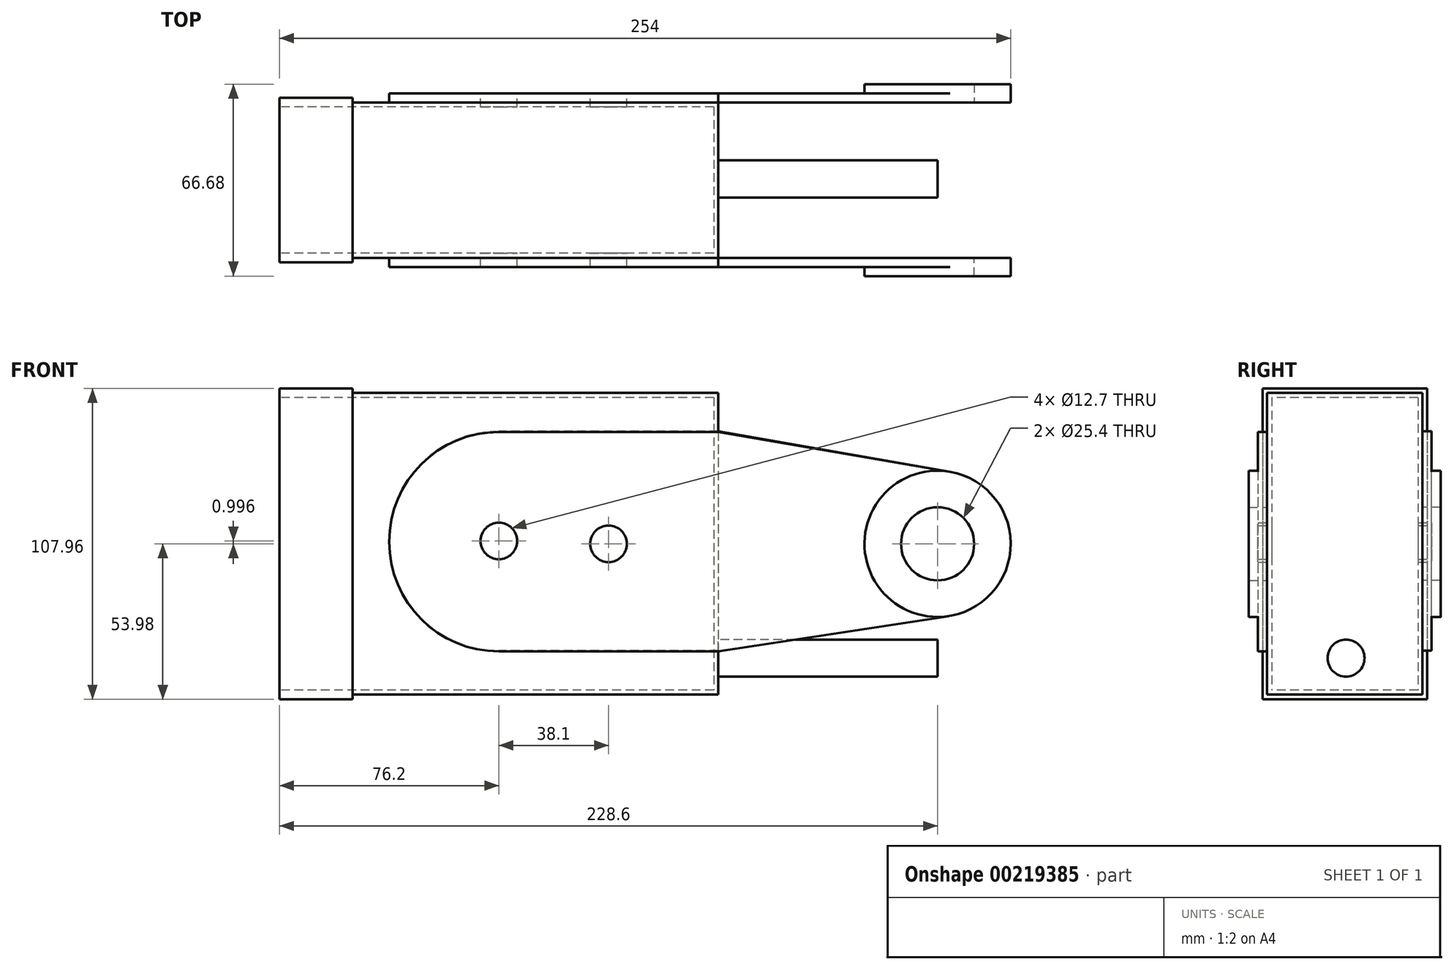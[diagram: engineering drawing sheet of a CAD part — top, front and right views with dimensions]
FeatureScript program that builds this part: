
annotation { "Feature Type Name" : "Feature", "Feature Type Description" : "" }
export const myFeature = defineFeature(function(context is Context, id is Id, definition is map)
    precondition{}
    {
        {
            var Q0;
            Q0=qCreatedBy(makeId("Right.planeOp"),FACE);
            var sketch = newSketch(context, id + "F0", { "sketchPlane" : qUnion([Q0])});
            skLineSegment(sketch, "E0.bottom", {"start": v(25.4, 50.8) * mm, "end": v(-25.4, 50.8) * mm});
            skLineSegment(sketch, "E0.top", {"start": v(25.4, -50.8) * mm, "end": v(-25.4, -50.8) * mm});
            skLineSegment(sketch, "E0.left", {"start": v(25.4, 50.8) * mm, "end": v(25.4, -50.8) * mm});
            skLineSegment(sketch, "E0.right", {"start": v(-25.4, 50.8) * mm, "end": v(-25.4, -50.8) * mm});
            skPoint(sketch, "E0.middle", {"position": v(0, 0) * mm});
            skLineSegment(sketch, "E1.0", {"start": v(26.99, 52.39) * mm, "end": v(-26.99, 52.39) * mm});
            skLineSegment(sketch, "E1.1", {"start": v(26.99, 52.39) * mm, "end": v(26.99, -52.39) * mm});
            skLineSegment(sketch, "E1.2", {"start": v(26.99, -52.39) * mm, "end": v(-26.99, -52.39) * mm});
            skLineSegment(sketch, "E1.3", {"start": v(-26.99, 52.39) * mm, "end": v(-26.99, -52.39) * mm});
            skSolve(sketch);
        }
        {
            var Q0;
            Q0=makeQuery(id+"F0.imprint","IMPRINT",FACE,{"disambiguationData":[TD([[makeQuery(id+"F0.imprint","IMPRINT",EDGE,{"derivedFrom":sQuery(id+"F0.wireOp",EDGE,"E0.bottom")}),-1.0]])]});
            extrude(context, id + "F1", {"entities" : qUnion([Q0]), "depth" : 152.4 * mm});
        }
        {
            var Q0;
            Q0=makeQuery(id+"F1.opExtrude","SWEPT_FACE",FACE,{"disambiguationData":[OSD([sQuery(id+"F0.wireOp",EDGE,"E1.1")])]});
            var sketch = newSketch(context, id + "F2", { "sketchPlane" : qUnion([Q0])});
            skLineSegment(sketch, "E2", {"start": v(-76.2, 52.39) * mm, "end": v(-76.2, -52.39) * mm, "construction": true});
            skLineSegment(sketch, "E3", {"start": v(0, 0) * mm, "end": v(-152.4, 0) * mm, "construction": true});
            skLineSegment(sketch, "E4", {"start": v(-152.4, 0) * mm, "end": v(-304.8, 0) * mm});
            skCircle(sketch, "E5", {"center": v(-228.6, 0) * mm, "radius": 12.7 * mm});
            skCircle(sketch, "E6", {"center": v(-228.6, 0) * mm, "radius": 25.4 * mm});
            skLineSegment(sketch, "E7", {"start": v(-152.4, 39.1) * mm, "end": v(-232.97, 25.02) * mm});
            skLineSegment(sketch, "E8", {"start": v(-152.4, -37.1) * mm, "end": v(-232.36, -25.12) * mm});
            skLineSegment(sketch, "E9", {"start": v(-152.4, 39.1) * mm, "end": v(-76.2, 39.1) * mm});
            skLineSegment(sketch, "E10", {"start": v(-152.4, -37.1) * mm, "end": v(-76.2, -37.1) * mm});
            skArc(sketch, "E11", {"start": v(-76.2, -37.1) * mm, "mid": v(-38.1, 1) * mm, "end": v(-76.2, 39.1) * mm});
            skSolve(sketch);
        }
        {
            var Q0;
            Q0 = qSketchRegion(id + "F2", true);
            extrude(context, id + "F3", {"entities" : qUnion([Q0]), "operationType" : NewBodyOperationType.ADD, "depth" : 3.17 * mm});
        }
        {
            var Q0;
            Q0=makeQuery(id+"F1.opExtrude","SWEPT_FACE",FACE,{"disambiguationData":[OSD([sQuery(id+"F0.wireOp",EDGE,"E1.3")])]});
            var sketch = newSketch(context, id + "F4", { "sketchPlane" : qUnion([Q0])});
            skLineSegment(sketch, "E12", {"start": v(152.4, 0) * mm, "end": v(293.28, 0) * mm});
            skPoint(sketch, "E12.endSnap0", {"position": v(152.4, 0) * mm});
            skCircle(sketch, "E13", {"center": v(228.6, 0) * mm, "radius": 12.7 * mm});
            skCircle(sketch, "E14", {"center": v(228.6, 0) * mm, "radius": 25.4 * mm});
            skLineSegment(sketch, "E15", {"start": v(152.4, 38.84) * mm, "end": v(232.9, 25.03) * mm});
            skLineSegment(sketch, "E16", {"start": v(152.4, -37.36) * mm, "end": v(232.44, -25.1) * mm});
            skLineSegment(sketch, "E17", {"start": v(152.4, 38.84) * mm, "end": v(76.2, 38.84) * mm});
            skLineSegment(sketch, "E18", {"start": v(152.4, -37.36) * mm, "end": v(76.2, -37.36) * mm});
            skLineSegment(sketch, "E19", {"start": v(76.2, 38.84) * mm, "end": v(76.2, -37.36) * mm, "construction": true});
            skArc(sketch, "E20", {"start": v(76.2, 38.84) * mm, "mid": v(38.1, 0.74) * mm, "end": v(76.2, -37.36) * mm});
            skSolve(sketch);
        }
        {
            var Q0;
            Q0 = qSketchRegion(id + "F4", true);
            extrude(context, id + "F5", {"entities" : qUnion([Q0]), "operationType" : NewBodyOperationType.ADD, "depth" : 3.17 * mm});
        }
        {
            var Q0;
            Q0=qCreatedBy(makeId("Right.planeOp"),FACE);
            var sketch = newSketch(context, id + "F6", { "sketchPlane" : qUnion([Q0])});
            skLineSegment(sketch, "E21.0", {"start": v(28.58, 53.97) * mm, "end": v(-28.57, 53.97) * mm});
            skLineSegment(sketch, "E21.1", {"start": v(28.58, 53.97) * mm, "end": v(28.58, -53.98) * mm});
            skLineSegment(sketch, "E21.2", {"start": v(28.58, -53.98) * mm, "end": v(-28.58, -53.98) * mm});
            skLineSegment(sketch, "E21.3", {"start": v(-28.57, 53.97) * mm, "end": v(-28.58, -53.98) * mm});
            skLineSegment(sketch, "E22.0", {"start": v(26.99, 52.39) * mm, "end": v(-26.99, 52.39) * mm});
            skLineSegment(sketch, "E22.1", {"start": v(26.99, 52.39) * mm, "end": v(26.99, -52.39) * mm});
            skLineSegment(sketch, "E22.2", {"start": v(26.99, -52.39) * mm, "end": v(-26.99, -52.39) * mm});
            skLineSegment(sketch, "E22.3", {"start": v(-26.99, 52.39) * mm, "end": v(-26.99, -52.39) * mm});
            skSolve(sketch);
        }
        {
            var Q0;
            Q0=makeQuery(id+"F6.imprint","IMPRINT",FACE,{"disambiguationData":[TD([[makeQuery(id+"F6.imprint","IMPRINT",EDGE,{"derivedFrom":sQuery(id+"F6.wireOp",EDGE,"E21.0")}),1.0]])]});
            extrude(context, id + "F7", {"entities" : qUnion([Q0]), "operationType" : NewBodyOperationType.ADD, "depth" : 25.4 * mm});
        }
        {
            var Q0;
            Q0=makeQuery(id+"F3.opExtrude","CAP_FACE",FACE,{"disambiguationData":[OSD([sQuery(id+"F2.wireOp",EDGE,"E5"),sQuery(id+"F2.wireOp",EDGE,"E6"),sQuery(id+"F2.wireOp",EDGE,"E7"),sQuery(id+"F2.wireOp",EDGE,"E8"),sQuery(id+"F2.wireOp",EDGE,"E9"),sQuery(id+"F2.wireOp",EDGE,"E10"),sQuery(id+"F2.wireOp",EDGE,"E11")])],"isStart":false});
            var sketch = newSketch(context, id + "F8", { "sketchPlane" : qUnion([Q0])});
            skCircle(sketch, "E23", {"center": v(-114.3, 0) * mm, "radius": 6.35 * mm});
            skCircle(sketch, "E24", {"center": v(-76.2, 1) * mm, "radius": 6.35 * mm});
            skSolve(sketch);
        }
        {
            var Q0;
            Q0=makeQuery(id+"F8.imprint","IMPRINT",FACE,{"disambiguationData":[TD([[makeQuery(id+"F8.imprint","IMPRINT",EDGE,{"derivedFrom":sQuery(id+"F8.wireOp",EDGE,"E23")}),1.0]])]});
            var Q1;
            Q1=makeQuery(id+"F8.imprint","IMPRINT",FACE,{"disambiguationData":[TD([[makeQuery(id+"F8.imprint","IMPRINT",EDGE,{"derivedFrom":sQuery(id+"F8.wireOp",EDGE,"E24")}),1.0]])]});
            extrude(context, id + "F9", {"entities" : qUnion([Q0, Q1]), "operationType" : NewBodyOperationType.REMOVE, "oppositeDirection" : true, "depth" : 152.4 * mm});
        }
        {
            var Q0;
            Q0=makeQuery(id+"F1.opExtrude","CAP_FACE",FACE,{"disambiguationData":[OSD([sQuery(id+"F0.wireOp",EDGE,"E0.bottom"),sQuery(id+"F0.wireOp",EDGE,"E0.top"),sQuery(id+"F0.wireOp",EDGE,"E0.left"),sQuery(id+"F0.wireOp",EDGE,"E0.right"),sQuery(id+"F0.wireOp",EDGE,"E1.0"),sQuery(id+"F0.wireOp",EDGE,"E1.1"),sQuery(id+"F0.wireOp",EDGE,"E1.2"),sQuery(id+"F0.wireOp",EDGE,"E1.3")])],"isStart":false});
            var sketch = newSketch(context, id + "F10", { "sketchPlane" : qUnion([Q0])});
            skLineSegment(sketch, "E25.bottom", {"start": v(25.4, 50.8) * mm, "end": v(-25.4, 50.8) * mm});
            skLineSegment(sketch, "E25.top", {"start": v(25.4, -50.8) * mm, "end": v(-25.4, -50.8) * mm});
            skLineSegment(sketch, "E25.left", {"start": v(25.4, 50.8) * mm, "end": v(25.4, -50.8) * mm});
            skLineSegment(sketch, "E25.right", {"start": v(-25.4, 50.8) * mm, "end": v(-25.4, -50.8) * mm});
            skPoint(sketch, "E25.middle", {"position": v(0, 0) * mm});
            skSolve(sketch);
        }
        {
            var Q0;
            Q0 = qSketchRegion(id + "F10", true);
            extrude(context, id + "F11", {"entities" : qUnion([Q0]), "operationType" : NewBodyOperationType.ADD, "oppositeDirection" : true, "depth" : 1.59 * mm});
        }
        {
            var Q0;
            Q0=makeQuery(id+"F5.opExtrude","CAP_FACE",FACE,{"disambiguationData":[OSD([sQuery(id+"F4.wireOp",EDGE,"E13"),sQuery(id+"F4.wireOp",EDGE,"E14"),sQuery(id+"F4.wireOp",EDGE,"E15"),sQuery(id+"F4.wireOp",EDGE,"E16"),sQuery(id+"F4.wireOp",EDGE,"E17"),sQuery(id+"F4.wireOp",EDGE,"E18"),sQuery(id+"F4.wireOp",EDGE,"E20")])],"isStart":false});
            var sketch = newSketch(context, id + "F12", { "sketchPlane" : qUnion([Q0])});
            skCircle(sketch, "E26", {"center": v(228.6, 0) * mm, "radius": 25.4 * mm});
            skCircle(sketch, "E27", {"center": v(228.6, 0) * mm, "radius": 12.7 * mm});
            skSolve(sketch);
        }
        {
            var Q0;
            Q0 = qSketchRegion(id + "F12", true);
            extrude(context, id + "F13", {"entities" : qUnion([Q0]), "operationType" : NewBodyOperationType.ADD, "depth" : 3.17 * mm});
        }
        {
            var Q0;
            Q0=makeQuery(id+"F3.opExtrude","CAP_FACE",FACE,{"disambiguationData":[OSD([sQuery(id+"F2.wireOp",EDGE,"E5"),sQuery(id+"F2.wireOp",EDGE,"E6"),sQuery(id+"F2.wireOp",EDGE,"E7"),sQuery(id+"F2.wireOp",EDGE,"E8"),sQuery(id+"F2.wireOp",EDGE,"E9"),sQuery(id+"F2.wireOp",EDGE,"E10"),sQuery(id+"F2.wireOp",EDGE,"E11")])],"isStart":false});
            var sketch = newSketch(context, id + "F14", { "sketchPlane" : qUnion([Q0])});
            skCircle(sketch, "E28", {"center": v(-228.6, 0) * mm, "radius": 12.7 * mm});
            skCircle(sketch, "E29", {"center": v(-228.6, 0) * mm, "radius": 25.4 * mm});
            skSolve(sketch);
        }
        {
            var Q0;
            Q0=makeQuery(id+"F14.imprint","IMPRINT",FACE,{"disambiguationData":[TD([[makeQuery(id+"F14.imprint","IMPRINT",EDGE,{"derivedFrom":sQuery(id+"F14.wireOp",EDGE,"E28")}),-1.0]])]});
            extrude(context, id + "F15", {"entities" : qUnion([Q0]), "operationType" : NewBodyOperationType.ADD, "depth" : 3.17 * mm});
        }
        {
            var Q0;
            Q0=makeQuery(id+"F11.boolean.opBoolean","MERGE",FACE,{"derivedFrom":[makeQuery(id+"F1.opExtrude","CAP_FACE",FACE,{"disambiguationData":[OSD([sQuery(id+"F0.wireOp",EDGE,"E0.bottom"),sQuery(id+"F0.wireOp",EDGE,"E0.top"),sQuery(id+"F0.wireOp",EDGE,"E0.left"),sQuery(id+"F0.wireOp",EDGE,"E0.right"),sQuery(id+"F0.wireOp",EDGE,"E1.0"),sQuery(id+"F0.wireOp",EDGE,"E1.1"),sQuery(id+"F0.wireOp",EDGE,"E1.2"),sQuery(id+"F0.wireOp",EDGE,"E1.3")])],"isStart":false}),makeQuery(id+"F11.opExtrude","CAP_FACE",FACE,{"disambiguationData":[OSD([sQuery(id+"F10.wireOp",EDGE,"E25.bottom"),sQuery(id+"F10.wireOp",EDGE,"E25.top"),sQuery(id+"F10.wireOp",EDGE,"E25.left"),sQuery(id+"F10.wireOp",EDGE,"E25.right")])],"isStart":true})]});
            var sketch = newSketch(context, id + "F16", { "sketchPlane" : qUnion([Q0])});
            skCircle(sketch, "E30", {"center": v(0.41, -39.69) * mm, "radius": 6.43 * mm});
            skSolve(sketch);
        }
        {
            var Q0;
            Q0=makeQuery(id+"F16.imprint","IMPRINT",FACE,{"disambiguationData":[TD([[makeQuery(id+"F16.imprint","IMPRINT",EDGE,{"derivedFrom":sQuery(id+"F16.wireOp",EDGE,"E30")}),1.0]])]});
            extrude(context, id + "F17", {"entities" : qUnion([Q0]), "operationType" : NewBodyOperationType.ADD, "depth" : 76.2 * mm});
        }
    });
